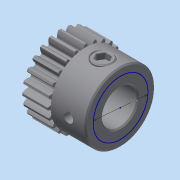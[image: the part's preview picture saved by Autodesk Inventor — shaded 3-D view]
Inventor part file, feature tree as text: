
AUTODESK INVENTOR PART (.ipt)
format: ipt  version: 2015 (Build 190159000, 159)  size: 1,085,952 bytes
history: native  units: in
note: dims shown in document units (in); Inventor stores cm internally (conversion verified against a paired STEP export)
features: imported_body x2, other x1, sketch x1
ambient origin geometry x8: Origin, YZ Plane, XZ Plane, XY Plane, X Axis, Y Axis, Z Axis, Center Point
bodies: Solid1 (feature_tree), Solid2 (feature_tree)
feature tree (4):
  other  "s1086z-048s0241"
  sketch  "Sketch1"  dims[d0=0.3937in]
  imported_body  "Base1"
  imported_body  "Base2"
